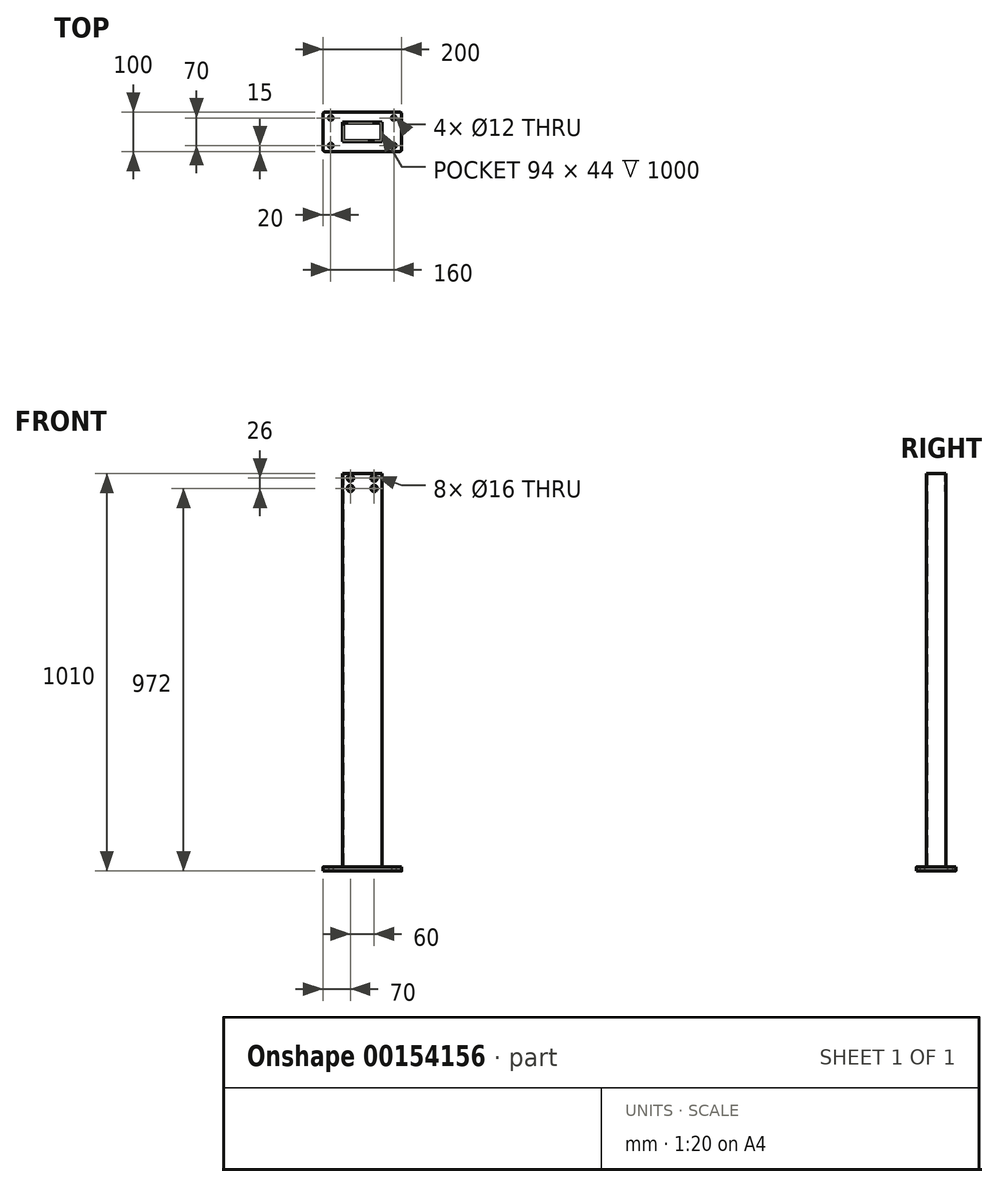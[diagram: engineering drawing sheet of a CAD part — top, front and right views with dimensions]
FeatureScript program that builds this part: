
annotation { "Feature Type Name" : "Feature", "Feature Type Description" : "" }
export const myFeature = defineFeature(function(context is Context, id is Id, definition is map)
    precondition{}
    {
        {
            var Q0;
            Q0=qCreatedBy(makeId("Top.planeOp"),FACE);
            var sketch = newSketch(context, id + "F0", { "sketchPlane" : qUnion([Q0])});
            skLineSegment(sketch, "E0.bottom", {"start": v(50, 25) * mm, "end": v(-50, 25) * mm});
            skLineSegment(sketch, "E0.top", {"start": v(50, -25) * mm, "end": v(-50, -25) * mm});
            skLineSegment(sketch, "E0.left", {"start": v(50, 25) * mm, "end": v(50, -25) * mm});
            skLineSegment(sketch, "E0.right", {"start": v(-50, 25) * mm, "end": v(-50, -25) * mm});
            skPoint(sketch, "E0.middle", {"position": v(0, 0) * mm});
            skLineSegment(sketch, "E1.bottom", {"start": v(47, 22) * mm, "end": v(-47, 22) * mm});
            skLineSegment(sketch, "E1.top", {"start": v(47, -22) * mm, "end": v(-47, -22) * mm});
            skLineSegment(sketch, "E1.left", {"start": v(47, 22) * mm, "end": v(47, -22) * mm});
            skLineSegment(sketch, "E1.right", {"start": v(-47, 22) * mm, "end": v(-47, -22) * mm});
            skSolve(sketch);
        }
        {
            var Q0;
            Q0 = qSketchRegion(id + "F0", true);
            extrude(context, id + "F1", {"entities" : qUnion([Q0]), "depth" : 1000 * mm});
        }
        {
            var Q0;
            Q0=qCreatedBy(makeId("Top.planeOp"),FACE);
            var sketch = newSketch(context, id + "F2", { "sketchPlane" : qUnion([Q0])});
            skLineSegment(sketch, "E2.bottom", {"start": v(100, -50) * mm, "end": v(-100, -50) * mm});
            skLineSegment(sketch, "E2.top", {"start": v(100, 50) * mm, "end": v(-100, 50) * mm});
            skLineSegment(sketch, "E2.left", {"start": v(100, -50) * mm, "end": v(100, 50) * mm});
            skLineSegment(sketch, "E2.right", {"start": v(-100, -50) * mm, "end": v(-100, 50) * mm});
            skPoint(sketch, "E2.middle", {"position": v(0, 0) * mm});
            skSolve(sketch);
        }
        {
            var Q0;
            Q0 = qSketchRegion(id + "F2", true);
            extrude(context, id + "F3", {"entities" : qUnion([Q0]), "operationType" : NewBodyOperationType.ADD, "oppositeDirection" : true, "depth" : 10 * mm});
        }
        {
            var Q0;
            Q0=makeQuery(id+"F3.opExtrude","CAP_FACE",FACE,{"disambiguationData":[OSD([sQuery(id+"F2.wireOp",EDGE,"E2.bottom"),sQuery(id+"F2.wireOp",EDGE,"E2.top"),sQuery(id+"F2.wireOp",EDGE,"E2.left"),sQuery(id+"F2.wireOp",EDGE,"E2.right")])],"isStart":false});
            var sketch = newSketch(context, id + "F4", { "sketchPlane" : qUnion([Q0])});
            skPoint(sketch, "E3", {"position": v(-80, 35) * mm});
            skPoint(sketch, "E4", {"position": v(-80, -35) * mm});
            skPoint(sketch, "E5", {"position": v(80, 35) * mm});
            skPoint(sketch, "E6", {"position": v(80, -35) * mm});
            skCircle(sketch, "E7", {"center": v(-80, 35) * mm, "radius": 6 * mm});
            skCircle(sketch, "E8", {"center": v(-80, -35) * mm, "radius": 6 * mm});
            skCircle(sketch, "E9", {"center": v(80, 35) * mm, "radius": 6 * mm});
            skCircle(sketch, "E10", {"center": v(80, -35) * mm, "radius": 6 * mm});
            skSolve(sketch);
        }
        {
            var Q0;
            Q0 = qSketchRegion(id + "F4", true);
            extrude(context, id + "F5", {"entities" : qUnion([Q0]), "operationType" : NewBodyOperationType.REMOVE, "oppositeDirection" : true, "depth" : 25 * mm});
        }
        {
            var Q0;
            Q0=makeQuery(id+"F3.opExtrude","SWEPT_EDGE",EDGE,{"disambiguationData":[OSD([sQuery(id+"F2.wireOp",EDGE,"E2.bottom"),sQuery(id+"F2.wireOp",EDGE,"E2.left")])]});
            var Q1;
            Q1=makeQuery(id+"F3.opExtrude","SWEPT_EDGE",EDGE,{"disambiguationData":[OSD([sQuery(id+"F2.wireOp",EDGE,"E2.top"),sQuery(id+"F2.wireOp",EDGE,"E2.left")])]});
            var Q2;
            Q2=makeQuery(id+"F3.opExtrude","SWEPT_EDGE",EDGE,{"disambiguationData":[OSD([sQuery(id+"F2.wireOp",EDGE,"E2.bottom"),sQuery(id+"F2.wireOp",EDGE,"E2.right")])]});
            var Q3;
            Q3=makeQuery(id+"F3.opExtrude","SWEPT_EDGE",EDGE,{"disambiguationData":[OSD([sQuery(id+"F2.wireOp",EDGE,"E2.top"),sQuery(id+"F2.wireOp",EDGE,"E2.right")])]});
            fillet(context, id + "F6", {"entities" : qUnion([Q0, Q1, Q2, Q3]), "radius" : 5 * mm, "tangentPropagation" : true, "allowEdgeOverflow" : false});
        }
        {
            var Q0;
            Q0=makeQuery(id+"F1.opExtrude","SWEPT_FACE",FACE,{"disambiguationData":[OSD([sQuery(id+"F0.wireOp",EDGE,"E0.top")])]});
            var sketch = newSketch(context, id + "F7", { "sketchPlane" : qUnion([Q0])});
            skPoint(sketch, "E11", {"position": v(-30, 988) * mm});
            skPoint(sketch, "E12", {"position": v(-30, 962) * mm});
            skPoint(sketch, "E13", {"position": v(30, 988) * mm});
            skPoint(sketch, "E14", {"position": v(30, 962) * mm});
            skCircle(sketch, "E15", {"center": v(-30, 988) * mm, "radius": 8 * mm});
            skCircle(sketch, "E16", {"center": v(30, 988) * mm, "radius": 8 * mm});
            skCircle(sketch, "E17", {"center": v(30, 962) * mm, "radius": 8 * mm});
            skCircle(sketch, "E18", {"center": v(-30, 962) * mm, "radius": 8 * mm});
            skSolve(sketch);
        }
        {
            var Q0;
            Q0 = qSketchRegion(id + "F7", true);
            extrude(context, id + "F8", {"entities" : qUnion([Q0]), "operationType" : NewBodyOperationType.REMOVE, "oppositeDirection" : true, "depth" : 50 * mm});
        }
    });
